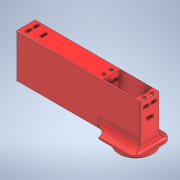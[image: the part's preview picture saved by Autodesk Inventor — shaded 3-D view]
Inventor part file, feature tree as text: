
AUTODESK INVENTOR PART (.ipt)
format: ipt  version: 2022 (Build 260153000, 153)  size: 1,272,832 bytes
history: native  units: mm
features: sketch x39, extrude x38, projected_geometry x14, fillet x13, other x10, pattern_circular x2, mirror x1
ambient origin geometry x8: Origin, YZ Plane, XZ Plane, XY Plane, X Axis, Y Axis, Z Axis, Center Point
bodies: Body1 (feature_tree)
feature tree (117):
  other  "Твердое тело1"
  extrude  "Выдавливание1"  Depth=29.25mm
  extrude  "Выдавливание2"  Depth=59.05mm
  extrude  "Выдавливание3"  Depth=15.0mm
  other  "РабПлоскость1"
  extrude  "Выдавливание4"  Depth=3.0mm
  other  "РабПлоскость2"
  other  "РабПлоскость3"
  other  "РабПлоскость5"
  extrude  "Выдавливание10"  Depth=41.0mm TaperAngle=0.0deg
  extrude  "Выдавливание11"  Depth=3.0mm TaperAngle=0.0deg
  fillet  "Сопряжение8"  Radius=4.2mm
  extrude  "Выдавливание12"  Depth=20.0mm TaperAngle=0.0deg
  fillet  "Сопряжение9"  [1 undecoded]
  mirror  "Зеркальное отражение2"
  extrude  "Выдавливание13"  Depth=7.15mm
  extrude  "Выдавливание15"  Depth=20.0mm
  sketch  "Эскиз18"
  other  "РабОсь1"
  extrude  "Выдавливание16"  Depth=3.25mm TaperAngle=0.0deg
  fillet  "Сопряжение12"  Radius=7.0mm
  pattern_circular  "Круговой массив1"  [2 undecoded]
  fillet  "Сопряжение14"  Radius=4.0mm
  extrude  "Выдавливание24"  Depth=1.95mm
  extrude  "Выдавливание25"  Depth=10.0mm
  extrude  "Выдавливание26"  Depth=2.0mm
  other  "РабПлоскость8"
  extrude  "Выдавливание27"  Depth=1.5mm TaperAngle=0.0deg
  extrude  "Выдавливание28"  Depth=1.0mm
  extrude  "Выдавливание29"  Depth=0.2mm
  extrude  "Выдавливание30"  Depth=19.0mm
  extrude  "Выдавливание31"  Depth=68.0mm
  extrude  "Выдавливание32"  Depth=3.5mm
  sketch  "Эскиз36"
  other  "РабТочка1"
  extrude  "Выдавливание33"  Depth=5.0mm
  extrude  "Выдавливание34"  Depth=4.1mm
  extrude  "Выдавливание35"  Depth=7.95mm
  extrude  "Выдавливание36"  Depth=28.1mm
  extrude  "Выдавливание37"  Depth=4.0mm TaperAngle=0.0deg
  other  "РабПлоскость9"
  extrude  "Выдавливание38"  Depth=18.75mm
  extrude  "Выдавливание39"  Depth=37.8mm
  extrude  "Выдавливание40"  Depth=2.0mm
  extrude  "Выдавливание41"  Depth=6.0mm TaperAngle=0.0deg
  extrude  "Выдавливание42"  Depth=0.5mm
  fillet  "Сопряжение21"  Radius=5.4mm
  fillet  "Сопряжение22"  Radius=0.7mm
  fillet  "Сопряжение23"  Radius=120.0mm
  extrude  "Выдавливание43"  Depth=1.5mm
  fillet  "Сопряжение24"  Radius=47.7mm
  pattern_circular  "Круговой массив2"  [2 undecoded]
  fillet  "Сопряжение25"  Radius=6.0mm
  extrude  "Выдавливание44"  Depth=1.5mm
  fillet  "Сопряжение26"  Radius=4.0mm
  extrude  "Выдавливание17"  Depth=4.0mm
  fillet  "Сопряжение15"  Radius=35.2mm
  extrude  "Выдавливание18"  Depth=9.8mm
  extrude  "Выдавливание19"  Depth=6.15mm
  extrude  "Выдавливание20"  Depth=5.8mm TaperAngle=0.0deg
  extrude  "Выдавливание21"  Depth=13.0mm
  fillet  "Сопряжение16"  Radius=1.9mm
  extrude  "Выдавливание22"  Depth=7.5mm
  other  "РабПлоскость7"
  extrude  "Выдавливание23"  Depth=4.8mm
  fillet  "Сопряжение17"  Radius=3.0mm
  sketch  "Эскиз14"
  sketch  "Эскиз1"
  sketch  "Эскиз2"
  sketch  "Эскиз3"
  sketch  "Эскиз4"
  sketch  "Эскиз10"
  sketch  "Эскиз11"
  sketch  "Эскиз13"
  sketch  "Эскиз15"
  sketch  "Эскиз17"
  sketch  "Эскиз19"
  projected_geometry  "Спроецированная петля1"
  sketch  "Эскиз20"
  projected_geometry  "Спроецированная петля2"
  sketch  "Эскиз21"
  projected_geometry  "Спроецированная петля3"
  sketch  "Эскиз22"
  sketch  "Эскиз23"
  sketch  "Эскиз25"
  projected_geometry  "Спроецированная петля4"
  sketch  "Эскиз26"
  projected_geometry  "Спроецированная петля5"
  sketch  "Эскиз27"
  projected_geometry  "Спроецированная петля6"
  sketch  "Эскиз28"
  projected_geometry  "Спроецированная петля7"
  sketch  "Эскиз29"
  projected_geometry  "Спроецированная петля8"
  sketch  "Эскиз31"
  projected_geometry  "Спроецированная петля9"
  sketch  "Эскиз32"
  sketch  "Эскиз33"
  sketch  "Эскиз34"
  sketch  "Эскиз35"
  sketch  "Эскиз37"
  projected_geometry  "Спроецированная петля10"
  sketch  "Эскиз38"
  sketch  "Эскиз39"
  sketch  "Эскиз40"
  sketch  "Эскиз41"
  sketch  "Эскиз42"
  projected_geometry  "Спроецированная петля11"
  sketch  "Эскиз43"
  sketch  "Эскиз44"
  projected_geometry  "Спроецированная петля12"
  sketch  "Эскиз45"
  projected_geometry  "Спроецированная петля13"
  projected_geometry  "Спроецированная петля14"
  sketch  "Эскиз46"
  sketch  "Эскиз47"
  sketch  "Эскиз48"
note: 5 required parameter values undecoded (feature->parameter linkage not recoverable at this tier; creation-order binding heuristic only, values carry confidence <= 0.55)
